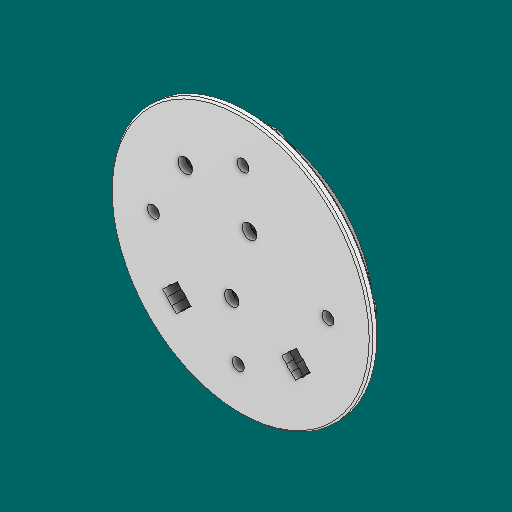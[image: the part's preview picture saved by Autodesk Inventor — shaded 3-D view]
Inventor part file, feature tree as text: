
AUTODESK INVENTOR PART (.ipt)
format: ipt  version: 2023.1 (Build 271208000, 208)  size: 1,399,296 bytes
history: native  units: in
note: dims shown in document units (in); Inventor stores cm internally (conversion verified against a paired STEP export)
features: extrude x6, sketch x6, projected_geometry x5, other x3, chamfer x2, reference x2, fillet x1
ambient origin geometry x8: Origin, YZ Plane, XZ Plane, XY Plane, X Axis, Y Axis, Z Axis, Center Point
bodies: Solid1 (feature_tree)
feature tree (25):
  extrude  "Extrusion1"  Depth=1.5748in TaperAngle=360.0deg
  extrude  "Extrusion2"  Depth=0.3in
  fillet  "Fillet1"  Radius=1.5748in
  extrude  "Extrusion4"  Depth=0.0472in
  chamfer  "Chamfer1"  Distance=0.1in
  chamfer  "Chamfer2"  Distance=0.0236in Angle=45.0deg
  extrude  "Extrusion5"  Depth=0.19in
  extrude  "Extrusion6"  Depth=0.3543in
  extrude  "Extrusion8"  Depth=0.3543in
  sketch  "Sketch1"  dims[d0=0.1562in d1=1.5748in d3=360.0deg]
  reference  "Reference1"
  reference  "Reference2"
  sketch  "Sketch2"  dims[d5=0.3in d6=0.0in d7=0.4724in d8=1.5748in d10=360.0deg]
  projected_geometry  "Projected Loop1"
  sketch  "Sketch4"  dims[d12=0.0472in d13=0.0in d14=0.25in]
  projected_geometry  "Projected Loop3"
  sketch  "Sketch5"  dims[d22=3.4in d23=0.1in d24=0.0in d25=0.0236in d26=0.125in d27=45.0deg]
  projected_geometry  "Projected Loop4"
  sketch  "Sketch6"  dims[d28=0.125in d29=0.125in d30=45.0deg d31=0.19in]
  projected_geometry  "Projected Loop5"
  sketch  "Sketch8"  dims[d32=0.1in d33=0.0in d34=0.33in d35=0.33in d36=0.33in d37=0.1in d38=0.0in d46=0.3543in d47=0.7874in d49=360.0deg d51=0.25in d52=1.0in d53=0.0in]
  projected_geometry  "Projected Loop7"
  other  "<userpath>\Documents\CAD\guardSwerve5\MainAssy.iam"
  other  "MainAssy.iam"
  other  "Carriage:1"
